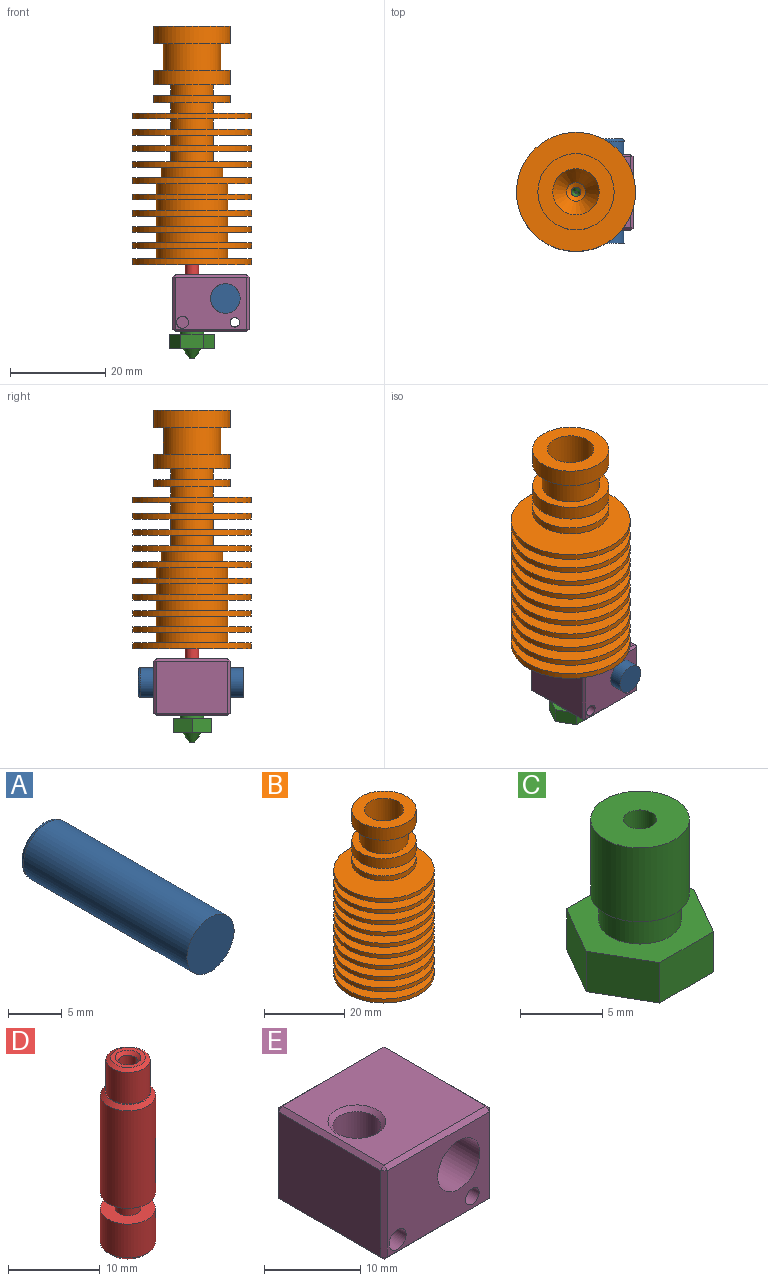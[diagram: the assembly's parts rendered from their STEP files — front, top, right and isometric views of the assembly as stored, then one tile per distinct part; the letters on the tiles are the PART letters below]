
ASSEMBLY  parts=5 mates=4
PART A: 4 faces, bbox 6.7x22x6.7 mm
  f0: cylinder r=3.1mm len=21.5mm, axis (0,1,0), area 418.8mm2, adj f2,f3
  f1: plane 5.2x5.2mm, normal (0,1,0), area 21.2mm2, adj f2
  f2: torus R=2.6mm, axis (0,-1,0), area 14.4mm2, adj f0,f1
  f3: plane 6.2x6.2mm, normal (0,-1,0), area 30.2mm2, adj f0
PART B: 58 faces, bbox 25x25x50.1 mm
  f0: plane 16x16mm, normal (0,0,1), area 137.4mm2, adj f1,f57
  f1: cylinder r=4.5mm len=9mm, axis (0,0,1), area 65mm2, adj f0,f2
  f2: plane 16x16mm, normal (0,0,-1), area 137.4mm2, adj f1,f41
  f3: plane 16x16mm, normal (0,0,1), area 88mm2, adj f40,f41
  f4: cylinder r=12.5mm len=25mm, axis (0,0,1), area 94.2mm2, adj f32,f35
  f5: cylinder r=7.5mm len=15mm, axis (0,0,1), area 103.7mm2, adj f35,f51
  f6: cylinder r=12.5mm len=25mm, axis (0,0,1), area 94.2mm2, adj f45,f46
  f7: cylinder r=12.5mm len=25mm, axis (0,0,1), area 94.2mm2, adj f43,f44
  f8: cylinder r=4.5mm len=9mm, axis (0,0,1), area 62.2mm2, adj f33,f43
  f9: cylinder r=4.5mm len=9mm, axis (0,0,1), area 62.2mm2, adj f44,f45
  f10: cylinder r=12.5mm len=25mm, axis (0,0,1), area 94.2mm2, adj f31,f51
  f11: cylinder r=7.5mm len=15mm, axis (0,0,1), area 103.7mm2, adj f31,f50
  f12: cylinder r=12.5mm len=25mm, axis (0,0,1), area 94.2mm2, adj f24,f26
  f13: cylinder r=7.5mm len=15mm, axis (0,0,1), area 103.7mm2, adj f26,f49
  f14: cylinder r=7.5mm len=15mm, axis (0,0,1), area 103.7mm2, adj f24,f25
  f15: cylinder r=12.5mm len=25mm, axis (0,0,1), area 94.2mm2, adj f27,f53
  f16: cylinder r=4.5mm len=9mm, axis (0,0,1), area 62.2mm2, adj f53,f56
  f17: cylinder r=4.5mm len=9mm, axis (0,0,1), area 62.2mm2, adj f27,f42
  f18: cylinder r=12.5mm len=25mm, axis (0,0,1), area 94.2mm2, adj f33,f42
  f19: cylinder r=12.5mm len=25mm, axis (0,0,1), area 94.2mm2, adj f36,f47
  f20: cylinder r=6.5mm len=13mm, axis (0,0,1), area 89.8mm2, adj f46,f47
  f21: cylinder r=7.5mm len=15mm, axis (0,0,1), area 103.7mm2, adj f36,f48
  f22: cylinder r=12.5mm len=25mm, axis (0,0,1), area 94.2mm2, adj f25,f50
  f23: cylinder r=12.5mm len=25mm, axis (0,0,1), area 94.2mm2, adj f48,f49
  f24: plane 25x25mm, normal (0,0,-1), area 314.2mm2, adj f12,f14
  f25: plane 25x25mm, normal (0,0,1), area 314.2mm2, adj f14,f22
  f26: plane 25x25mm, normal (0,0,1), area 314.2mm2, adj f12,f13
  f27: plane 25x25mm, normal (0,0,-1), area 427.3mm2, adj f15,f17
  f28: cylinder r=1mm len=11.41mm, axis (0,0,1), area 71.7mm2, adj f34,f55
  f29: plane 16x16mm, normal (0,0,1), area 126.7mm2, adj f30,f38
  f30: cylinder r=8mm len=16mm, axis (0,0,1), area 186mm2, adj f29,f39
  f31: plane 25x25mm, normal (0,0,1), area 314.2mm2, adj f10,f11
  f32: plane 25x25mm, normal (0,0,-1), area 462.6mm2, adj f4,f54
  f33: plane 25x25mm, normal (0,0,-1), area 427.3mm2, adj f8,f18
  f34: cone r=2mm half-angle=60deg, axis (0,0,1), area 10.9mm2, adj f28,f52
  f35: plane 25x25mm, normal (0,0,1), area 314.2mm2, adj f4,f5
  f36: plane 25x25mm, normal (0,0,-1), area 314.2mm2, adj f19,f21
  f37: cone r=4.86mm half-angle=30deg, axis (0,0,1), area 123.5mm2, adj f38,f52
  f38: cylinder r=4.86mm len=10mm, axis (0,0,1), area 305.6mm2, adj f29,f37
  f39: plane 16x16mm, normal (0,0,-1), area 88mm2, adj f30,f40
  f40: cylinder r=6mm len=12mm, axis (0,0,1), area 211.1mm2, adj f3,f39
  f41: cylinder r=8mm len=16mm, axis (0,0,1), area 150.8mm2, adj f2,f3
  f42: plane 25x25mm, normal (0,0,1), area 427.3mm2, adj f17,f18
  f43: plane 25x25mm, normal (0,0,1), area 427.3mm2, adj f7,f8
  f44: plane 25x25mm, normal (0,0,-1), area 427.3mm2, adj f7,f9
  f45: plane 25x25mm, normal (0,0,1), area 427.3mm2, adj f6,f9
  f46: plane 25x25mm, normal (0,0,-1), area 358.1mm2, adj f6,f20
  f47: plane 25x25mm, normal (0,0,1), area 358.1mm2, adj f19,f20
  f48: plane 25x25mm, normal (0,0,1), area 314.2mm2, adj f21,f23
  f49: plane 25x25mm, normal (0,0,-1), area 314.2mm2, adj f13,f23
  f50: plane 25x25mm, normal (0,0,-1), area 314.2mm2, adj f11,f22
  f51: plane 25x25mm, normal (0,0,-1), area 314.2mm2, adj f5,f10
  f52: cylinder r=2mm len=4mm, axis (0,0,1), area 50.3mm2, adj f34,f37
  f53: plane 25x25mm, normal (0,0,1), area 427.3mm2, adj f15,f16
  f54: cylinder r=3mm len=18mm, axis (0,0,1), area 339.3mm2, adj f32,f55
  f55: cone r=1mm half-angle=60deg, axis (0,0,-1), area 29mm2, adj f28,f54
  f56: plane 16x16mm, normal (0,0,-1), area 137.4mm2, adj f16,f57
  f57: cylinder r=8mm len=16mm, axis (0,0,1), area 75.4mm2, adj f0,f56
PART C: 16 faces, bbox 9.2x8x12.5 mm
  f0: cone r=0.6mm half-angle=35deg, axis (0,0,1), area 19.9mm2, adj f6,f15
  f1: cone r=1mm half-angle=21.2deg, axis (0,0,1), area 8.3mm2, adj f4,f15
  f2: cylinder r=3mm len=6mm, axis (0,0,1), area 103.7mm2, adj f13,f14
  f3: cylinder r=2.5mm len=5mm, axis (0,0,1), area 31.4mm2, adj f5,f13
  f4: cylinder r=1mm len=10.5mm, axis (0,0,1), area 66mm2, adj f1,f14
  f5: plane 9.24x8mm, normal (0,0,1), area 35.8mm2, adj f3,f7,f8,f9,f10,f11,f12
  f6: plane 9.24x8mm, normal (0,0,-1), area 42.9mm2, adj f0,f7,f8,f9,f10,f11,f12
  f7: plane 4x3mm, normal (0.87,0.5,0), area 13.9mm2, adj f5,f6,f8,f12
  f8: plane 4.62x3mm, normal (0,1,0), area 13.9mm2, adj f5,f6,f7,f9
  f9: plane 4x3mm, normal (-0.87,0.5,0), area 13.9mm2, adj f5,f6,f8,f10
  f10: plane 4x3mm, normal (-0.87,-0.5,0), area 13.9mm2, adj f5,f6,f9,f11
  f11: plane 4.62x3mm, normal (0,-1,0), area 13.9mm2, adj f5,f6,f10,f12
  f12: plane 4x3mm, normal (0.87,-0.5,0), area 13.9mm2, adj f5,f6,f7,f11
  f13: plane 6x6mm, normal (0,0,-1), area 8.6mm2, adj f2,f3
  f14: plane 6x6mm, normal (0,0,1), area 25.1mm2, adj f2,f4
  f15: plane 1.2x1.2mm, normal (0,0,-1), area 1mm2, adj f0,f1
PART D: 14 faces, bbox 6x6x25.1 mm
  f0: plane 3.8x3.8mm, normal (0,0,1), area 5.2mm2, adj f2,f3
  f1: cylinder r=1mm len=24.7mm, axis (0,0,1), area 155.2mm2, adj f2,f10
  f2: cone r=1mm half-angle=45deg, axis (0,0,1), area 4.3mm2, adj f0,f1
  f3: cone r=1.9mm half-angle=60deg, axis (0,0,-1), area 7.8mm2, adj f0,f4
  f4: cylinder r=2.4mm len=4.8mm, axis (0,0,1), area 63.5mm2, adj f3,f13
  f5: cone r=2.5mm half-angle=45deg, axis (0,0,-1), area 12.2mm2, adj f6,f13
  f6: cylinder r=3mm len=13mm, axis (0,0,1), area 245mm2, adj f5,f12
  f7: cylinder r=1.4mm len=2.8mm, axis (0,0,1), area 18.5mm2, adj f11,f12
  f8: cylinder r=3mm len=6mm, axis (0,0,1), area 84.8mm2, adj f9,f11
  f9: cone r=3mm half-angle=45deg, axis (0,0,1), area 12.2mm2, adj f8,f10
  f10: plane 5x5mm, normal (0,0,-1), area 16.5mm2, adj f1,f9
  f11: plane 6x6mm, normal (0,0,1), area 22.1mm2, adj f7,f8
  f12: plane 6x6mm, normal (0,0,-1), area 22.1mm2, adj f6,f7
  f13: plane 5x5mm, normal (0,0,1), area 1.5mm2, adj f4,f5
PART E: 35 faces, bbox 16x16x12 mm
  f0: cylinder r=3.1mm len=16mm, axis (0,1,0), area 306.3mm2, adj f1,f14,f28
  f1: cylinder r=1.25mm len=3.57mm, axis (0,0,1), area 28mm2, adj f0,f12
  f2: cylinder r=2.5mm len=11mm, axis (0,0,-1), area 172.8mm2, adj f11,f23
  f3: plane 15x0.5mm, normal (0.71,0,-0.71), area 10.6mm2, adj f9,f13,f19,f31
  f4: plane 0.5x0.5mm, normal (0.58,0.58,0.58), area 0.2mm2, adj f15,f22,f32
  f5: cylinder r=1.25mm len=4.5mm, axis (0,1,0), area 35.3mm2, adj f28,f29
  f6: plane 15x15mm, normal (0,0,1), area 196.7mm2, adj f11,f15,f26,f32,f33
  f7: plane 0.5x0.5mm, normal (-0.58,0.58,0.58), area 0.2mm2, adj f18,f32,f33
  f8: plane 0.5x0.5mm, normal (0.58,-0.58,0.58), area 0.2mm2, adj f10,f15,f26
  f9: plane 0.5x0.5mm, normal (0.58,-0.58,-0.58), area 0.2mm2, adj f3,f10,f24
  f10: plane 11x0.5mm, normal (0.71,-0.71,0), area 7.8mm2, adj f8,f9,f19,f28
  f11: cone r=2.5mm half-angle=45deg, axis (0,0,1), area 12.2mm2, adj f2,f6
  f12: cone r=1.25mm half-angle=45deg, axis (0,0,-1), area 6.7mm2, adj f1,f13
  f13: plane 15x15mm, normal (0,0,-1), area 187.1mm2, adj f3,f12,f21,f23,f24,f27
  f14: plane 15x11mm, normal (0,1,0), area 131.7mm2, adj f0,f18,f20,f21,f22,f32
  f15: plane 15x0.5mm, normal (0.71,0,0.71), area 10.6mm2, adj f4,f6,f8,f19
  f16: plane 15x11mm, normal (-1,0,0), area 165mm2, adj f18,f27,f30,f33
  f17: plane 0.5x0.5mm, normal (-0.58,-0.58,-0.58), area 0.2mm2, adj f24,f27,f30
  f18: plane 11x0.5mm, normal (-0.71,0.71,0), area 7.8mm2, adj f7,f14,f16,f34
  f19: plane 15x11mm, normal (1,0,0), area 165mm2, adj f3,f10,f15,f22
  f20: cylinder r=1mm len=16mm, axis (0,1,0), area 100.5mm2, adj f14,f28
  f21: plane 15x0.5mm, normal (0,0.71,-0.71), area 10.6mm2, adj f13,f14,f31,f34
  f22: plane 11x0.5mm, normal (0.71,0.71,0), area 7.8mm2, adj f4,f14,f19,f31
  f23: cone r=3mm half-angle=45deg, axis (0,0,-1), area 12.2mm2, adj f2,f13
  f24: plane 15x0.5mm, normal (0,-0.71,-0.71), area 10.6mm2, adj f9,f13,f17,f28
  f25: plane 0.5x0.5mm, normal (-0.58,-0.58,0.58), area 0.2mm2, adj f26,f30,f33
  f26: plane 15x0.5mm, normal (0,-0.71,0.71), area 10.6mm2, adj f6,f8,f25,f28
  f27: plane 15x0.5mm, normal (-0.71,0,-0.71), area 10.6mm2, adj f13,f16,f17,f34
  f28: plane 15x11mm, normal (0,-1,0), area 126.8mm2, adj f0,f5,f10,f20,f24,f26,f30
  f29: plane 2.5x2.5mm, normal (0,-1,0), area 4.9mm2, adj f5
  f30: plane 11x0.5mm, normal (-0.71,-0.71,0), area 7.8mm2, adj f16,f17,f25,f28
  f31: plane 0.5x0.5mm, normal (0.58,0.58,-0.58), area 0.2mm2, adj f3,f21,f22
  f32: plane 15x0.5mm, normal (0,0.71,0.71), area 10.6mm2, adj f4,f6,f7,f14
  f33: plane 15x0.5mm, normal (-0.71,0,0.71), area 10.6mm2, adj f6,f7,f16,f25
  f34: plane 0.5x0.5mm, normal (-0.58,0.58,-0.58), area 0.2mm2, adj f18,f21,f27
PLACE A t=(3.31,0.95,1.36)mm
PLACE B t=(3.31,-0.3,1.36)mm
PLACE C t=(3.31,-0.3,0.86)mm
PLACE D t=(3.31,-0.3,1.36)mm
PLACE E t=(3.31,-0.3,1.36)mm
MATE fastened C.f0 <-> D.f1  axis (0,0,1) through (-0.69,-0.3,8.36)mm
MATE fastened A.f0 <-> E.f0  axis (0,1,0) through (6.31,-0.3,8.36)mm
MATE fastened E.f2 <-> D.f1  axis (0,0,1) through (-0.69,-0.3,13.36)mm
MATE fastened D.f1 <-> B.f1  axis (0,0,-1) through (-0.69,-0.3,15.46)mm
